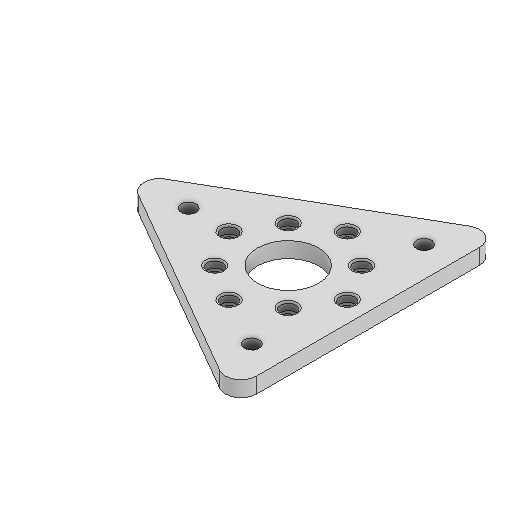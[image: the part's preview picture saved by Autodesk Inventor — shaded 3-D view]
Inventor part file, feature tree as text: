
AUTODESK INVENTOR PART (.ipt)
format: ipt  version: 2025.1 (Build 291241020, 241B)  size: 306,176 bytes
history: native  units: in
note: dims shown in document units (in); Inventor stores cm internally (conversion verified against a paired STEP export)
features: sketch x4, extrude x3, fillet x2
ambient origin geometry x8: Origin, YZ Plane, XZ Plane, XY Plane, X Axis, Y Axis, Z Axis, Center Point
bodies: Solid1 (feature_tree)
feature tree (9):
  extrude  "Extrusion1"  Depth=4.0415in
  fillet  "Fillet1"  Radius=4.0415in
  sketch  "Sketch3"  dims[d5=120.0deg d6=120.0deg d7=0.3937in d8=0.0in]
  extrude  "Extrusion2"  Depth=0.481in
  extrude  "Extrusion3"  TaperAngle=120.0deg  [1 undecoded]
  fillet  "Fillet2"  Radius=0.3937in
  sketch  "Sketch Circular Pattern1"  dims[d0=7.0in d1=1.5472in d2=4.0415in]
  sketch  "Sketch Circular Pattern2"  dims[d3=2.5161in d4=0.481in]
  sketch  "Sketch Circular Pattern3"  dims[d9=0.3937in d11=0.0203in d13=7.874in d15=360.0deg d17=1.1811in d19=360.0deg d21=0.2244in d22=0.2244in d23=1.8559in d24=1.8559in d25=0.928in d26=0.928in d27=0.2244in d28=4.358in d35=0.3937in d36=0.0in d41=0.3937in d47=0.1969in d48=0.0in d49=0.0394in d51=1.4961in d52=1.4961in d53=1.4961in d54=1.4961in d55=0.377in d56=2.5161in d57=1.1811in d59=360.0deg]
note: 1 required parameter value undecoded (feature->parameter linkage not recoverable at this tier; creation-order binding heuristic only, values carry confidence <= 0.55)
